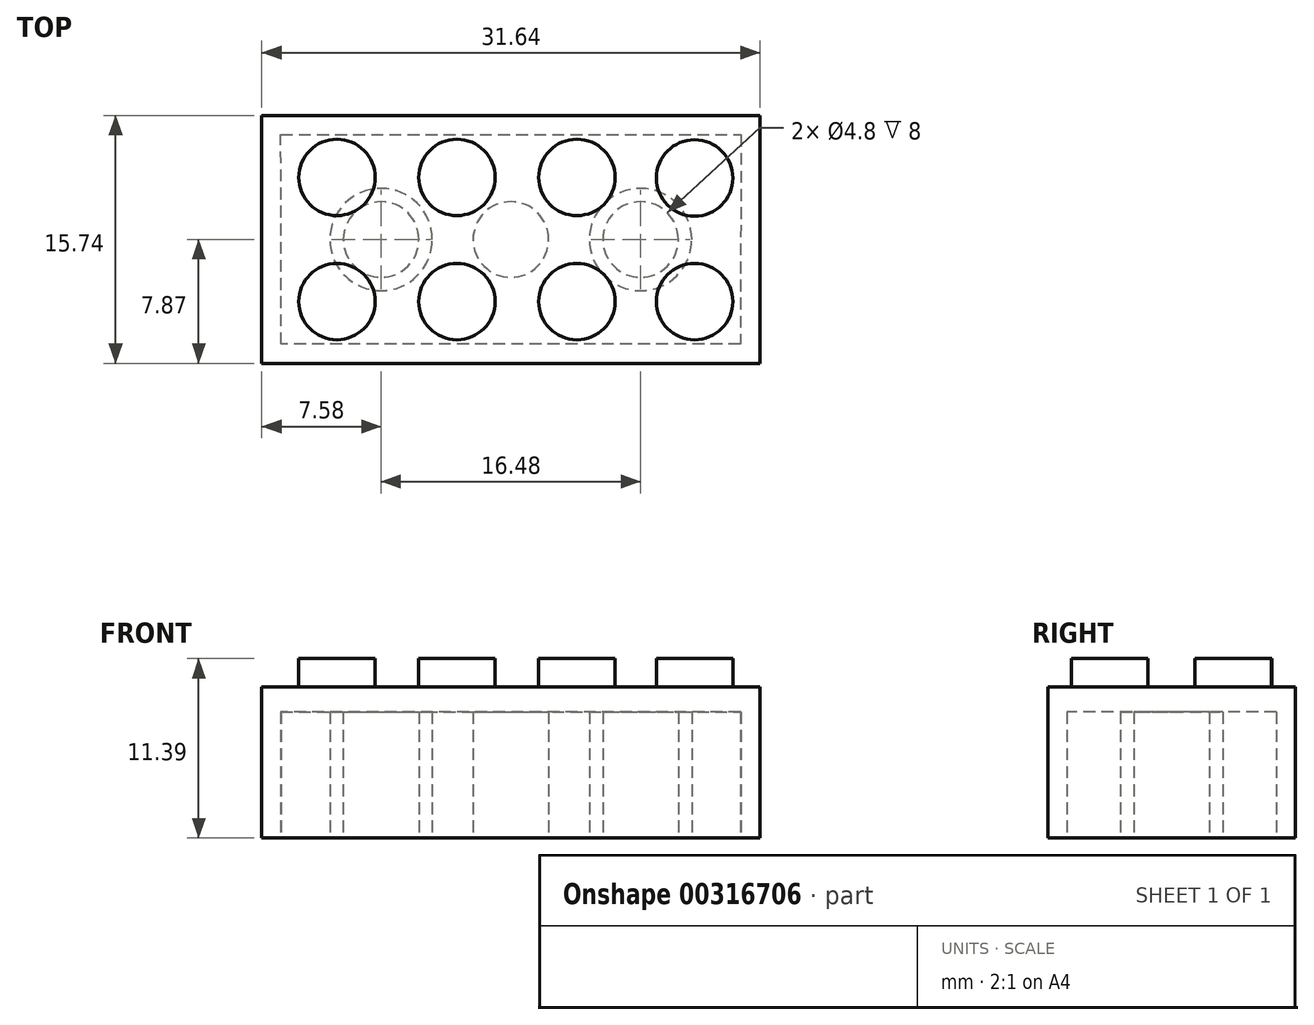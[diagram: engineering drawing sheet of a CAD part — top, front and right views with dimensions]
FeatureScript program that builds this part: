
annotation { "Feature Type Name" : "Feature", "Feature Type Description" : "" }
export const myFeature = defineFeature(function(context is Context, id is Id, definition is map)
    precondition{}
    {
        {
            var Q0;
            Q0=qCreatedBy(makeId("Top.planeOp"),FACE);
            var sketch = newSketch(context, id + "F0", { "sketchPlane" : qUnion([Q0])});
            skLineSegment(sketch, "E0.bottom", {"start": v(0, 0) * mm, "end": v(31.64, 0) * mm});
            skLineSegment(sketch, "E0.top", {"start": v(0, 15.74) * mm, "end": v(31.64, 15.74) * mm});
            skLineSegment(sketch, "E0.left", {"start": v(0, 0) * mm, "end": v(0, 15.74) * mm});
            skLineSegment(sketch, "E0.right", {"start": v(31.64, 0) * mm, "end": v(31.64, 15.74) * mm});
            skSolve(sketch);
        }
        {
            var Q0;
            Q0=makeQuery(id+"F0.imprint","IMPRINT",FACE,{"disambiguationData":[TD([[makeQuery(id+"F0.imprint","IMPRINT",EDGE,{"derivedFrom":sQuery(id+"F0.wireOp",EDGE,"E0.bottom")}),1.0]])]});
            extrude(context, id + "F1", {"entities" : qUnion([Q0]), "depth" : 9.6 * mm});
        }
        {
            var Q0;
            Q0=makeQuery(id+"F1.opExtrude","CAP_FACE",FACE,{"disambiguationData":[OSD([sQuery(id+"F0.wireOp",EDGE,"E0.bottom"),sQuery(id+"F0.wireOp",EDGE,"E0.top"),sQuery(id+"F0.wireOp",EDGE,"E0.left"),sQuery(id+"F0.wireOp",EDGE,"E0.right")])],"isStart":false});
            var sketch = newSketch(context, id + "F2", { "sketchPlane" : qUnion([Q0])});
            skCircle(sketch, "E1", {"center": v(4.77, 11.82) * mm, "radius": 2.43 * mm});
            skCircle(sketch, "E2", {"center": v(12.4, 11.82) * mm, "radius": 2.43 * mm});
            skCircle(sketch, "E3", {"center": v(20.02, 11.82) * mm, "radius": 2.43 * mm});
            skCircle(sketch, "E4", {"center": v(27.49, 11.78) * mm, "radius": 2.43 * mm});
            skCircle(sketch, "E5", {"center": v(4.77, 3.92) * mm, "radius": 2.43 * mm});
            skCircle(sketch, "E6", {"center": v(12.4, 3.92) * mm, "radius": 2.43 * mm});
            skCircle(sketch, "E7", {"center": v(20.02, 3.92) * mm, "radius": 2.43 * mm});
            skCircle(sketch, "E8", {"center": v(27.49, 3.92) * mm, "radius": 2.43 * mm});
            skLineSegment(sketch, "E9", {"start": v(0, 15.74) * mm, "end": v(31.64, 15.74) * mm});
            skSolve(sketch);
        }
        {
            var Q0;
            Q0=makeQuery(id+"F2.imprint","IMPRINT",FACE,{"disambiguationData":[TD([[makeQuery(id+"F2.imprint","IMPRINT",EDGE,{"derivedFrom":sQuery(id+"F2.wireOp",EDGE,"E1")}),1.0]])]});
            var Q1;
            Q1=makeQuery(id+"F2.imprint","IMPRINT",FACE,{"disambiguationData":[TD([[makeQuery(id+"F2.imprint","IMPRINT",EDGE,{"derivedFrom":sQuery(id+"F2.wireOp",EDGE,"E2")}),1.0]])]});
            var Q2;
            Q2=makeQuery(id+"F2.imprint","IMPRINT",FACE,{"disambiguationData":[TD([[makeQuery(id+"F2.imprint","IMPRINT",EDGE,{"derivedFrom":sQuery(id+"F2.wireOp",EDGE,"E3")}),1.0]])]});
            var Q3;
            Q3=makeQuery(id+"F2.imprint","IMPRINT",FACE,{"disambiguationData":[TD([[makeQuery(id+"F2.imprint","IMPRINT",EDGE,{"derivedFrom":sQuery(id+"F2.wireOp",EDGE,"E4")}),1.0]])]});
            var Q4;
            Q4=makeQuery(id+"F2.imprint","IMPRINT",FACE,{"disambiguationData":[TD([[makeQuery(id+"F2.imprint","IMPRINT",EDGE,{"derivedFrom":sQuery(id+"F2.wireOp",EDGE,"E5")}),1.0]])]});
            var Q5;
            Q5=makeQuery(id+"F2.imprint","IMPRINT",FACE,{"disambiguationData":[TD([[makeQuery(id+"F2.imprint","IMPRINT",EDGE,{"derivedFrom":sQuery(id+"F2.wireOp",EDGE,"E6")}),1.0]])]});
            var Q6;
            Q6=makeQuery(id+"F2.imprint","IMPRINT",FACE,{"disambiguationData":[TD([[makeQuery(id+"F2.imprint","IMPRINT",EDGE,{"derivedFrom":sQuery(id+"F2.wireOp",EDGE,"E7")}),1.0]])]});
            var Q7;
            Q7=makeQuery(id+"F2.imprint","IMPRINT",FACE,{"disambiguationData":[TD([[makeQuery(id+"F2.imprint","IMPRINT",EDGE,{"derivedFrom":sQuery(id+"F2.wireOp",EDGE,"E8")}),1.0]])]});
            extrude(context, id + "F3", {"entities" : qUnion([Q0, Q1, Q2, Q3, Q4, Q5, Q6, Q7]), "operationType" : NewBodyOperationType.ADD, "depth" : 1.8 * mm});
        }
        {
            var Q0;
            Q0=makeQuery(id+"F1.opExtrude","CAP_FACE",FACE,{"disambiguationData":[OSD([sQuery(id+"F0.wireOp",EDGE,"E0.bottom"),sQuery(id+"F0.wireOp",EDGE,"E0.top"),sQuery(id+"F0.wireOp",EDGE,"E0.left"),sQuery(id+"F0.wireOp",EDGE,"E0.right")])],"isStart":true});
            var sketch = newSketch(context, id + "F4", { "sketchPlane" : qUnion([Q0])});
            skLineSegment(sketch, "E10", {"start": v(0, -7.87) * mm, "end": v(31.64, -7.87) * mm});
            skCircle(sketch, "E11", {"center": v(15.82, -7.87) * mm, "radius": 3.25 * mm});
            skCircle(sketch, "E12", {"center": v(7.58, -7.87) * mm, "radius": 3.25 * mm});
            skCircle(sketch, "E13", {"center": v(24.06, -7.87) * mm, "radius": 3.25 * mm});
            skLineSegment(sketch, "E14", {"start": v(1.2, -14.52) * mm, "end": v(30.44, -14.52) * mm});
            skLineSegment(sketch, "E15", {"start": v(1.23, -1.22) * mm, "end": v(1.2, -14.52) * mm});
            skLineSegment(sketch, "E16", {"start": v(30.4, -1.22) * mm, "end": v(1.23, -1.22) * mm});
            skLineSegment(sketch, "E17", {"start": v(30.44, -14.52) * mm, "end": v(30.4, -1.22) * mm});
            skLineSegment(sketch, "E18", {"start": v(15.82, -1.22) * mm, "end": v(15.82, -4.62) * mm});
            skLineSegment(sketch, "E19", {"start": v(15.82, -14.52) * mm, "end": v(15.82, -11.12) * mm});
            skCircle(sketch, "E20", {"center": v(15.82, -7.87) * mm, "radius": 2.4 * mm});
            skCircle(sketch, "E21", {"center": v(24.06, -7.87) * mm, "radius": 2.4 * mm});
            skCircle(sketch, "E22", {"center": v(7.58, -7.87) * mm, "radius": 2.4 * mm});
            skSolve(sketch);
        }
        {
            var Q0;
            {var subQ4=sQuery(id+"F4.wireOp",EDGE,"E19");Q0=makeQuery(id+"F4.imprint","IMPRINT",FACE,{"disambiguationData":[TD([[makeQuery(id+"F4.imprint","IMPRINT",EDGE,{"derivedFrom":subQ4}),-1.0]])]});}
            var Q1;
            {var subQ4=sQuery(id+"F4.wireOp",EDGE,"E18");Q1=makeQuery(id+"F4.imprint","IMPRINT",FACE,{"disambiguationData":[TD([[makeQuery(id+"F4.imprint","IMPRINT",EDGE,{"derivedFrom":subQ4}),1.0]])]});}
            var Q2;
            {var subQ6=sQuery(id+"F4.wireOp",EDGE,"E18");Q2=makeQuery(id+"F4.imprint","IMPRINT",FACE,{"disambiguationData":[TD([[makeQuery(id+"F4.imprint","IMPRINT",EDGE,{"derivedFrom":subQ6}),-1.0]])]});}
            var Q3;
            {var subQ0=sQuery(id+"F4.wireOp",EDGE,"E19");Q3=makeQuery(id+"F4.imprint","IMPRINT",FACE,{"disambiguationData":[TD([[makeQuery(id+"F4.imprint","IMPRINT",EDGE,{"derivedFrom":subQ0}),1.0]])]});}
            var Q4;
            {var subQ0=sQuery(id+"F4.wireOp",EDGE,"E22");var subQ1=sQuery(id+"F4.wireOp",EDGE,"E10");var subQ2=makeQuery(id+"F4.imprint","INTERSECT",VERTEX,{"disambiguationData":[OD(0.0)],"derivedFrom":[subQ1,subQ0]});Q4=makeQuery(id+"F4.imprint","IMPRINT",FACE,{"disambiguationData":[TD([[makeQuery(id+"F4.imprint","IMPRINT",EDGE,{"disambiguationData":[TD([[subQ2,-1.0]])],"derivedFrom":subQ1}),1.0]])]});}
            var Q5;
            {var subQ0=sQuery(id+"F4.wireOp",EDGE,"E22");var subQ1=sQuery(id+"F4.wireOp",EDGE,"E10");var subQ2=makeQuery(id+"F4.imprint","INTERSECT",VERTEX,{"disambiguationData":[OD(0.0)],"derivedFrom":[subQ1,subQ0]});Q5=makeQuery(id+"F4.imprint","IMPRINT",FACE,{"disambiguationData":[TD([[makeQuery(id+"F4.imprint","IMPRINT",EDGE,{"disambiguationData":[TD([[subQ2,-1.0]])],"derivedFrom":subQ1}),-1.0]])]});}
            var Q6;
            {var subQ0=sQuery(id+"F4.wireOp",EDGE,"E20");var subQ1=sQuery(id+"F4.wireOp",EDGE,"E10");var subQ2=makeQuery(id+"F4.imprint","INTERSECT",VERTEX,{"disambiguationData":[OD(0.0)],"derivedFrom":[subQ1,subQ0]});Q6=makeQuery(id+"F4.imprint","IMPRINT",FACE,{"disambiguationData":[TD([[makeQuery(id+"F4.imprint","IMPRINT",EDGE,{"disambiguationData":[TD([[subQ2,-1.0]])],"derivedFrom":subQ1}),-1.0]])]});}
            var Q7;
            {var subQ0=sQuery(id+"F4.wireOp",EDGE,"E20");var subQ1=sQuery(id+"F4.wireOp",EDGE,"E10");var subQ2=makeQuery(id+"F4.imprint","INTERSECT",VERTEX,{"disambiguationData":[OD(0.0)],"derivedFrom":[subQ1,subQ0]});Q7=makeQuery(id+"F4.imprint","IMPRINT",FACE,{"disambiguationData":[TD([[makeQuery(id+"F4.imprint","IMPRINT",EDGE,{"disambiguationData":[TD([[subQ2,-1.0]])],"derivedFrom":subQ1}),1.0]])]});}
            var Q8;
            {var subQ0=sQuery(id+"F4.wireOp",EDGE,"E21");var subQ1=sQuery(id+"F4.wireOp",EDGE,"E10");var subQ2=makeQuery(id+"F4.imprint","INTERSECT",VERTEX,{"disambiguationData":[OD(0.0)],"derivedFrom":[subQ1,subQ0]});Q8=makeQuery(id+"F4.imprint","IMPRINT",FACE,{"disambiguationData":[TD([[makeQuery(id+"F4.imprint","IMPRINT",EDGE,{"disambiguationData":[TD([[subQ2,-1.0]])],"derivedFrom":subQ1}),1.0]])]});}
            var Q9;
            {var subQ0=sQuery(id+"F4.wireOp",EDGE,"E21");var subQ1=sQuery(id+"F4.wireOp",EDGE,"E10");var subQ2=makeQuery(id+"F4.imprint","INTERSECT",VERTEX,{"disambiguationData":[OD(0.0)],"derivedFrom":[subQ1,subQ0]});Q9=makeQuery(id+"F4.imprint","IMPRINT",FACE,{"disambiguationData":[TD([[makeQuery(id+"F4.imprint","IMPRINT",EDGE,{"disambiguationData":[TD([[subQ2,-1.0]])],"derivedFrom":subQ1}),-1.0]])]});}
            extrude(context, id + "F5", {"entities" : qUnion([Q0, Q1, Q2, Q3, Q4, Q5, Q6, Q7, Q8, Q9]), "operationType" : NewBodyOperationType.REMOVE, "oppositeDirection" : true, "depth" : 8 * mm});
        }
    });
